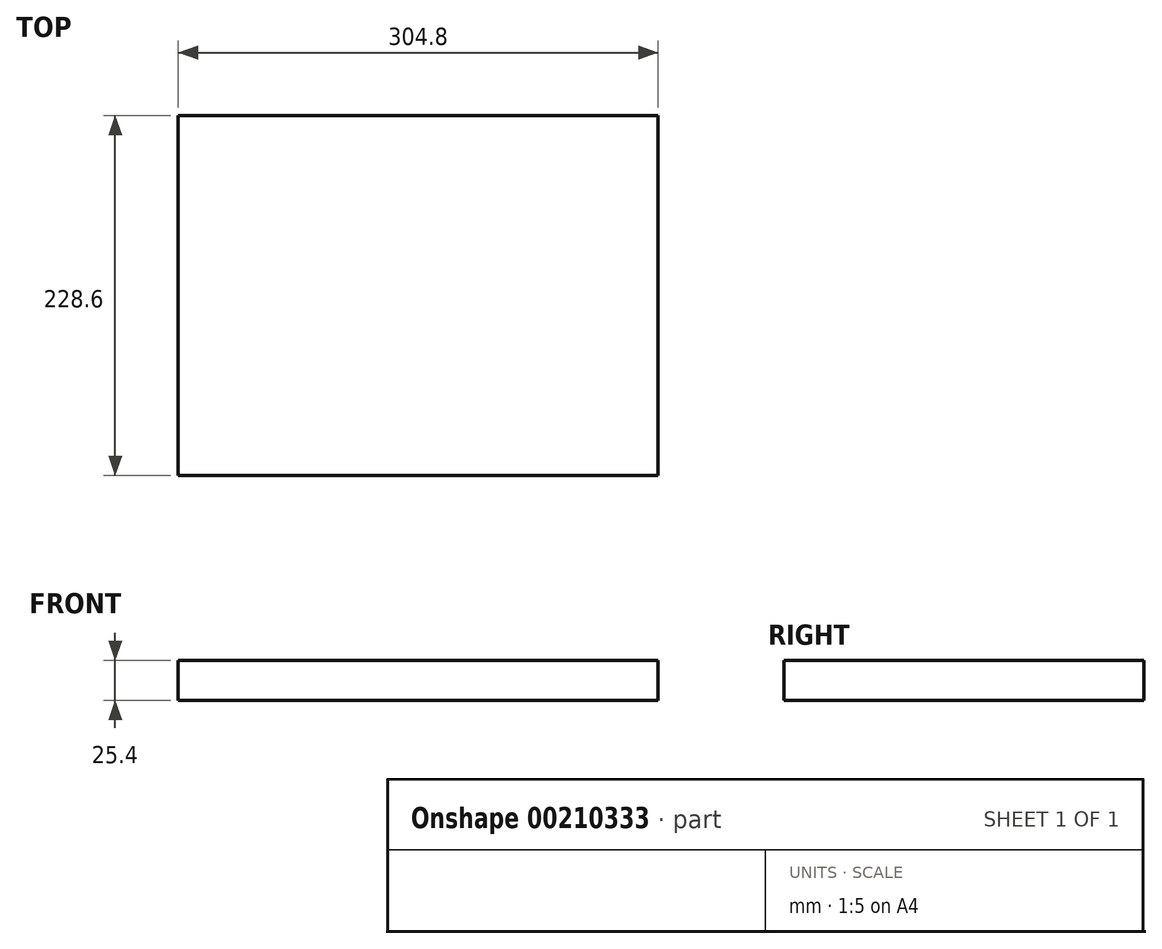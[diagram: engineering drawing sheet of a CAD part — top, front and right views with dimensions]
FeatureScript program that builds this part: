
annotation { "Feature Type Name" : "Feature", "Feature Type Description" : "" }
export const myFeature = defineFeature(function(context is Context, id is Id, definition is map)
    precondition{}
    {
        {
            var Q0;
            Q0=qCreatedBy(makeId("Top.planeOp"),FACE);
            var sketch = newSketch(context, id + "F0", { "sketchPlane" : qUnion([Q0])});
            skLineSegment(sketch, "E0.bottom", {"start": v(152.4, 114.3) * mm, "end": v(-152.4, 114.3) * mm});
            skLineSegment(sketch, "E0.top", {"start": v(152.4, -114.3) * mm, "end": v(-152.4, -114.3) * mm});
            skLineSegment(sketch, "E0.left", {"start": v(152.4, 114.3) * mm, "end": v(152.4, -114.3) * mm});
            skLineSegment(sketch, "E0.right", {"start": v(-152.4, 114.3) * mm, "end": v(-152.4, -114.3) * mm});
            skPoint(sketch, "E0.middle", {"position": v(0, 0) * mm});
            skSolve(sketch);
        }
        {
            var Q0;
            Q0 = qSketchRegion(id + "F0", true);
            extrude(context, id + "F1", {"entities" : qUnion([Q0]), "depth" : 25.4 * mm});
        }
    });
